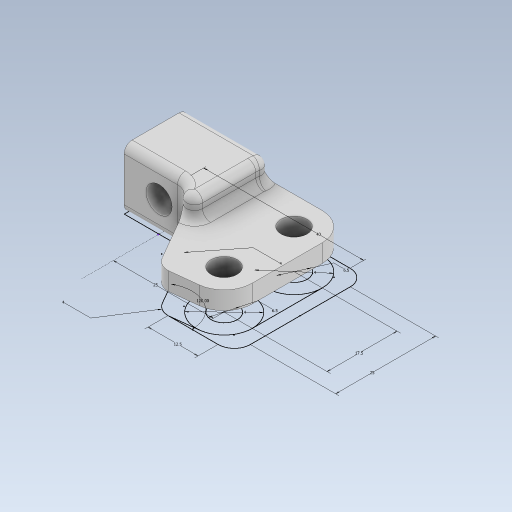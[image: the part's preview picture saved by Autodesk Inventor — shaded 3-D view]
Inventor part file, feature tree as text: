
AUTODESK INVENTOR PART (.ipt)
format: ipt  version: 2023 (Build 270158000, 158)  size: 465,920 bytes
history: native  units: in
note: dims shown in document units (in); Inventor stores cm internally (conversion verified against a paired STEP export)
features: extrude x3, fillet x3, sketch x2, plane x1, mirror x1, projected_geometry x1
ambient origin geometry x8: Origin, YZ Plane, XZ Plane, XY Plane, X Axis, Y Axis, Z Axis, Center Point
bodies: Solid1 (feature_tree)
feature tree (11):
  extrude  "Extrusion1"  Depth=0.2559in
  extrude  "Extrusion2"  Depth=0.1575in
  fillet  "Fillet1"  Radius=0.9843in
  fillet  "Fillet2"  Radius=0.4921in
  plane  "Work Plane1"
  mirror  "Mirror1"
  fillet  "Fillet3"  Radius=1.5748in
  extrude  "Extrusion4"  Depth=0.0787in
  sketch  "Sketch1"  dims[d0=0.689in d1=0.2559in]
  projected_geometry  "Projected Loop1"
  sketch  "Sketch4"  dims[d2=0.2559in d3=0.1575in d4=0.9843in d5=0.4921in d6=1.5748in d7=0.9843in d8=0.5906in d9=0.0in d10=0.1575in d11=120.0deg d12=0.2067in d13=0.0in d14=0.0787in d15=0.0787in d16=-0.0886in d20=0.0787in d21=0.5512in d22=0.5512in d23=0.2559in d24=0.0in d25=0.0in]
